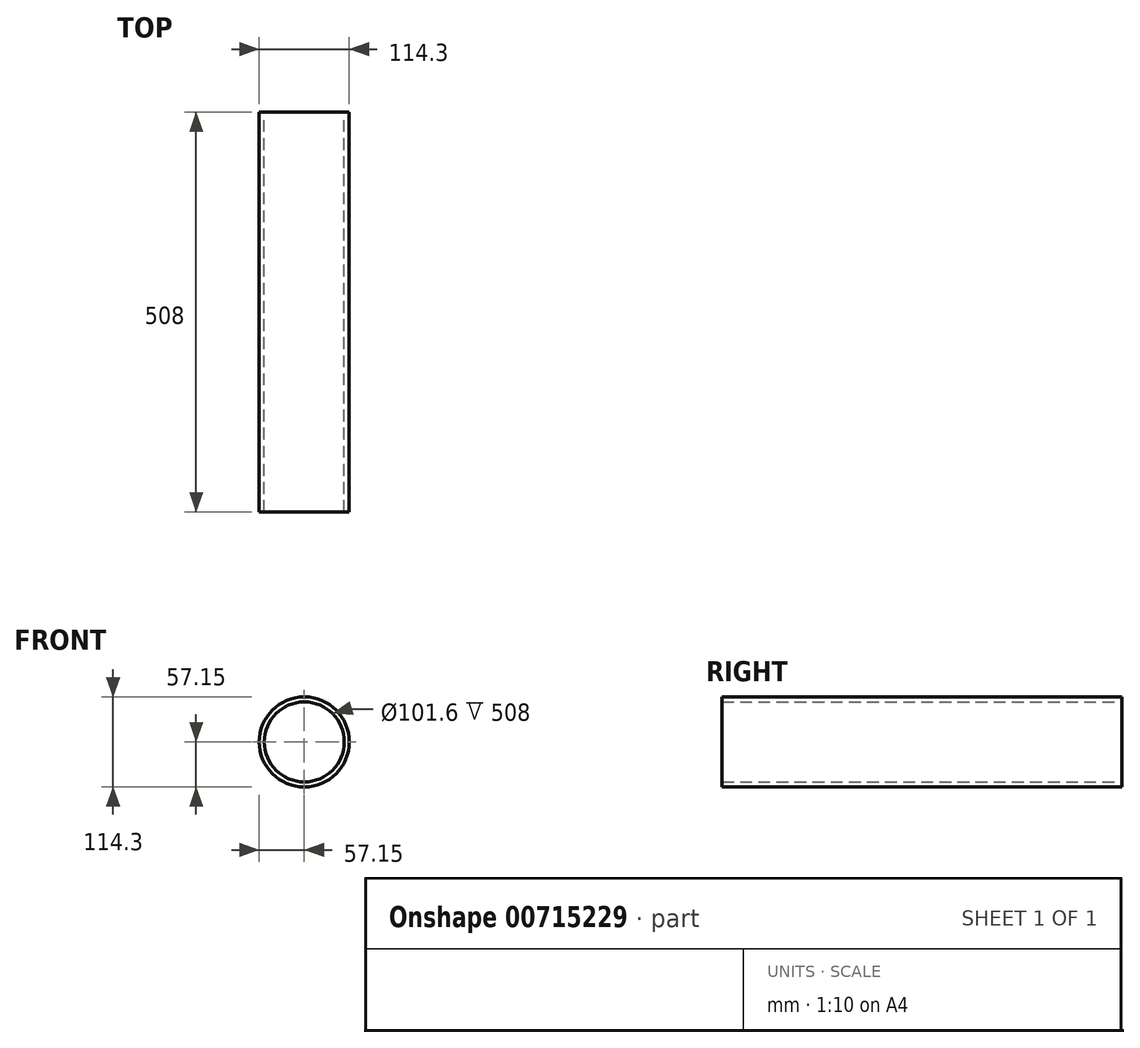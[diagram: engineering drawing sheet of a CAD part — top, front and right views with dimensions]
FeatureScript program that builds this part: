
annotation { "Feature Type Name" : "Feature", "Feature Type Description" : "" }
export const myFeature = defineFeature(function(context is Context, id is Id, definition is map)
    precondition{}
    {
        {
            var Q0;
            Q0=qCreatedBy(makeId("Front.planeOp"),FACE);
            var sketch = newSketch(context, id + "F0", { "sketchPlane" : qUnion([Q0])});
            skCircle(sketch, "E0", {"center": v(0, 0) * mm, "radius": 50.8 * mm});
            skCircle(sketch, "E1", {"center": v(0, 0) * mm, "radius": 57.15 * mm});
            skSolve(sketch);
        }
        {
            var Q0;
            Q0 = qSketchRegion(id + "F0", true);
            extrude(context, id + "F1", {"entities" : qUnion([Q0]), "endBound" : BoundingType.SYMMETRIC, "depth" : 508 * mm, "offsetDistance" : 25.4 * mm});
        }
    });
